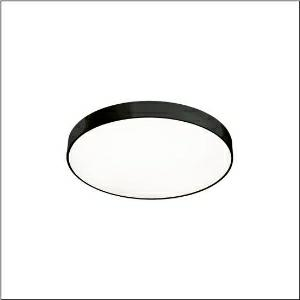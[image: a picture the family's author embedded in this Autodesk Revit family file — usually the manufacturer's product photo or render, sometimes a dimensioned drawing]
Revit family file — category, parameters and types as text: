
# Revit family: round_21_m_51mr36gd0321b
name_source: partatom
category: Lighting Fixtures
units: mm (PartAtom-declared; Revit-internal decimal feet)

## family parameters
Cut with Voids When Loaded = No
Host = Face
Light Source = No
Part Type = Normal
Room Calculation Point = No
Round Connector Dimension = Use Diameter
Shared = No

## types (1)
- Round 21 M (1 x LED, 7550 lm, 54.6 W, 3000K)
    Apparent Load = 55 VA
    CIE Flux Codes = 49 80 96 85 100
    Color Rendering = 80
    Color Temperature = 3000K
    Default Elevation = 1800 mm
    Description = Round 21 M, wall and ceiling luminaire, primary optical cover: cover, of PMMA, opal, light emission: direct/indirect distribution, primary light characteristic: symmetric, installation type: suspended mounting, surface-mounted, LED, rated luminous flux: 7.550lm, luminous efficacy: 138lm/W, light colour: 830, colour temperature: 3000K, control gear: DALI 2, with terminal, 5-pole, mains connection: 230V, AC, 50/60Hz, rated input power: 54.6W, housing, of aluminium, coated, black, diameter: 600mm, height: 62mm, protection rating (complete): IP40, insulation class (complete): insulation class I (protective earthing), certification: CE, impact resistance: IK04, permissible operating ambient temperature: -10..+35°C, packaging unit: 1 piece
    Height = 87 mm
    Lamp = 1 x LED
    Lamp Light Flux = 7550 lm
    Lamp Power = 54.6 W
    Lamp count = 1
    Length = 600 mm
    Luminous efficacy = 138 lm/W
    Manufacturer = Siteco
    ModVariant = No
    Model = 51MR36GD0321B
    Mounting Place = Ceiling
    Mounting Type = Surface mounted
    Number of Poles = 1
    OnlyDefault = Yes
    Power Factor = 1
    Product Name = Round 21 M
    Product group = wall and ceiling luminaire
    ProductGroupID = 304
    Protection Class = Protection class I
    Protection Degree = IP 40
    RLX_Detail_Level = 1
    RLX_Emergency_Light_Flux = 0 lm
    RLX_Emergency_Type = 0
    RLX_Emergency_Type_DB = No
    RlxData = <blob elided: 18133 chars, md5=6f6d494b>
    Socket = socket
    Standby Power = 0 W
    System Light Flux = 7550 lm
    System Power = 55 W
    Type Comments = Product without accessories
    Type Image = l_1258332.jpg
    URL = http://relux.com
    VarID = ---
    Voltage = 0 V
    Weight = 0.00 kg
    Width = 0 mm  [stored 0 ft]

note: [stored X ft] marks values corroborated as IEEE doubles in the binary element streams (Revit-internal decimal feet)

## geometry (parser evidence)
native form markers: Blend x4, Sweep x12
no freeform markers — native parametric forms only
